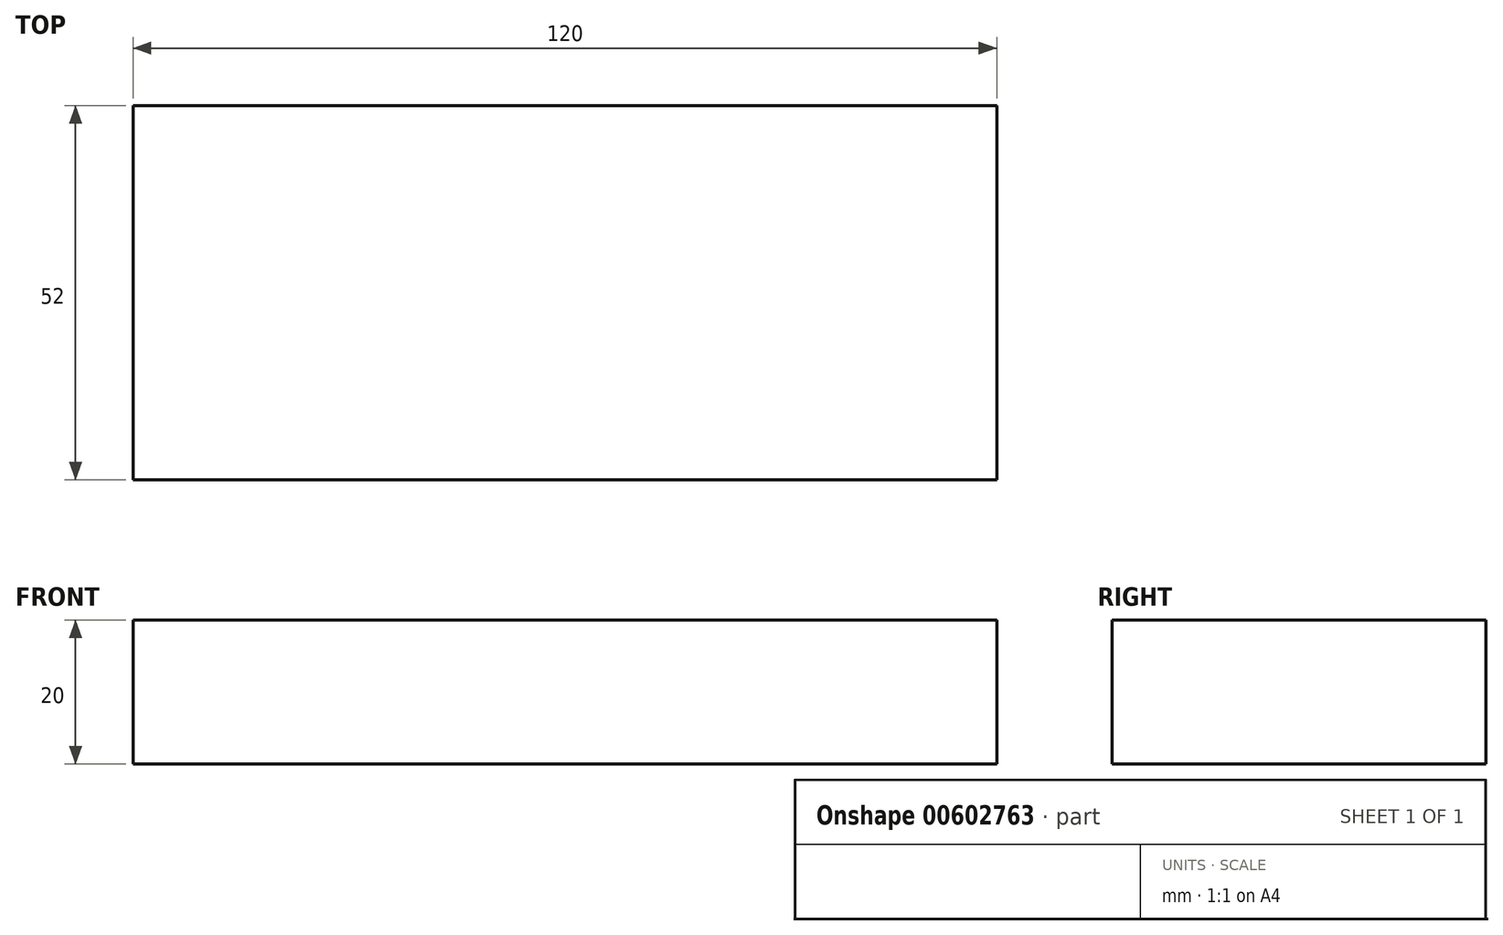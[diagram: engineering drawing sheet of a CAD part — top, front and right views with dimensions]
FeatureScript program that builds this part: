
annotation { "Feature Type Name" : "Feature", "Feature Type Description" : "" }
export const myFeature = defineFeature(function(context is Context, id is Id, definition is map)
    precondition{}
    {
        {
            var Q0;
            Q0=qCreatedBy(makeId("Front.planeOp"),FACE);
            var sketch = newSketch(context, id + "F0", { "sketchPlane" : qUnion([Q0])});
            skLineSegment(sketch, "E0.bottom", {"start": v(-56.53, 17.65) * mm, "end": v(63.47, 17.65) * mm});
            skLineSegment(sketch, "E0.top", {"start": v(-56.53, 37.65) * mm, "end": v(63.47, 37.65) * mm});
            skLineSegment(sketch, "E0.left", {"start": v(-56.53, 17.65) * mm, "end": v(-56.53, 37.65) * mm});
            skLineSegment(sketch, "E0.right", {"start": v(63.47, 17.65) * mm, "end": v(63.47, 37.65) * mm});
            skSolve(sketch);
        }
        {
            var Q0;
            Q0=makeQuery(id+"F0.imprint","IMPRINT",FACE,{"disambiguationData":[TD([[makeQuery(id+"F0.imprint","IMPRINT",EDGE,{"derivedFrom":sQuery(id+"F0.wireOp",EDGE,"E0.bottom")}),1.0]])]});
            extrude(context, id + "F1", {"entities" : qUnion([Q0]), "depth" : 52 * mm, "offsetDistance" : 25 * mm});
        }
    });
